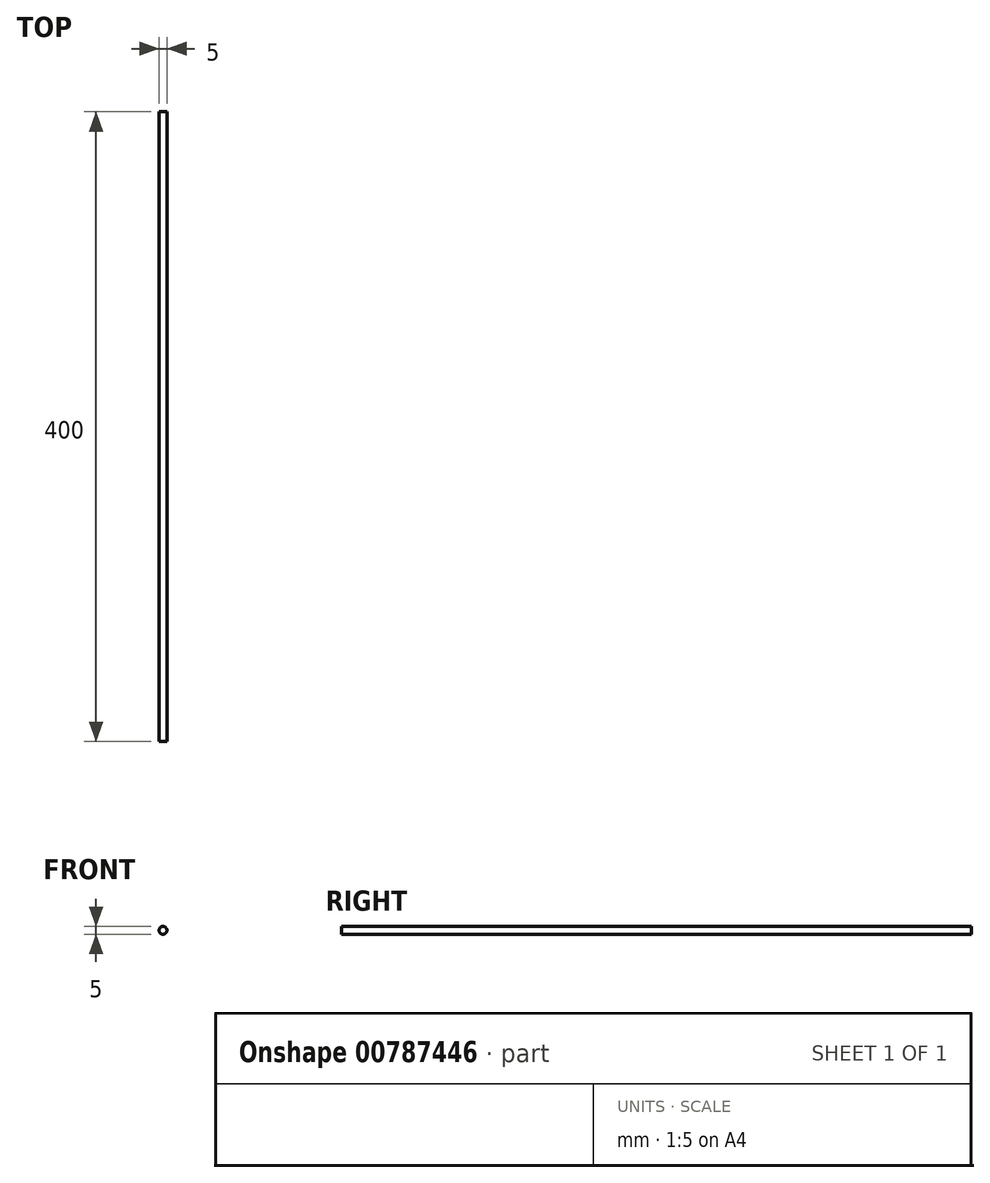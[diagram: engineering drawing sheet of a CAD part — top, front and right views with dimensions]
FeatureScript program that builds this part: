
annotation { "Feature Type Name" : "Feature", "Feature Type Description" : "" }
export const myFeature = defineFeature(function(context is Context, id is Id, definition is map)
    precondition{}
    {
        {
            var Q0;
            Q0=qCreatedBy(makeId("Front.planeOp"),FACE);
            var sketch = newSketch(context, id + "F0", { "sketchPlane" : qUnion([Q0])});
            skCircle(sketch, "E0", {"center": v(0, 0) * mm, "radius": 2.5 * mm});
            skSolve(sketch);
        }
        {
            var Q0;
            Q0 = qSketchRegion(id + "F0", true);
            extrude(context, id + "F1", {"entities" : qUnion([Q0]), "endBound" : BoundingType.SYMMETRIC, "depth" : 400 * mm, "offsetDistance" : 25 * mm});
        }
    });
